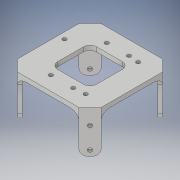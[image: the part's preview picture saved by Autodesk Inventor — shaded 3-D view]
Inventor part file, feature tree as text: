
AUTODESK INVENTOR PART (.ipt)
format: ipt  version: 2019 (Build 230136000, 136)  size: 287,232 bytes
history: native  units: mm
features: sketch x7, projected_geometry x5, hole x4, fillet x4, extrude x3, chamfer x1
ambient origin geometry x8: Origin, YZ Plane, XZ Plane, XY Plane, X Axis, Y Axis, Z Axis, Center Point
bodies: Solid1 (feature_tree)
feature tree (24):
  extrude  "Extrusion1"  Depth=4.0mm
  chamfer  "Chamfer2"  Distance=4.0mm
  extrude  "Extrusion4"  Depth=10.0mm
  hole  "Hole4"  [1 undecoded]
  fillet  "Fillet3"  Radius=19.0mm
  hole  "Hole5"  [1 undecoded]
  fillet  "Fillet4"  Radius=14.0mm
  fillet  "Fillet5"  Radius=19.0mm
  hole  "Hole7"  [1 undecoded]
  extrude  "Extrusion5"  Depth=6.0mm
  fillet  "Fillet6"  Radius=68.6mm
  hole  "Hole8"  [1 undecoded]
  sketch  "Sketch1"  dims[d0=75.0mm d1=75.0mm d2=4.0mm d3=0.0mm]
  sketch  "Sketch11"  dims[d66=10.0mm d67=2.0mm d68=45.0deg d69=3.0mm]
  projected_geometry  "Projected Loop11"
  sketch  "Sketch12"  dims[d70=34.0mm d71=0.0mm d72=14.0mm d73=19.0mm]
  projected_geometry  "Projected Loop12"
  sketch  "Sketch13"  dims[d74=3.5mm d75=6.0mm d76=4.0mm d77=2.0mm d78=90.0deg d79=8.0mm d80=0.0mm d81=4.0mm d82=14.0mm d83=19.0mm]
  projected_geometry  "Projected Loop13"
  sketch  "Sketch15"  dims[d84=3.5mm d85=6.0mm d86=4.0mm d87=2.0mm d88=90.0deg d89=8.0mm d90=0.0mm d91=6.0mm]
  sketch  "Sketch16"  dims[d92=6.0mm d108=53.3mm d109=68.6mm]
  projected_geometry  "Projected Loop15"
  sketch  "Sketch17"  dims[d110=15.3mm d111=2.5mm d112=14.0mm d113=2.5mm d117=2.5mm d118=15.2mm d119=3.5mm d120=6.0mm d121=4.0mm d122=2.0mm d123=90.0deg d124=8.0mm d125=0.0mm d126=35.0mm d127=35.0mm d128=35.0mm d129=0.0mm d130=6.0mm d132=50.0mm d133=50.0mm d134=10.0mm d135=10.0mm d136=3.5mm d137=6.0mm d138=4.0mm d139=2.0mm d140=90.0deg d141=8.0mm d142=0.0mm]
  projected_geometry  "Projected Loop16"
note: 4 required parameter values undecoded (feature->parameter linkage not recoverable at this tier; creation-order binding heuristic only, values carry confidence <= 0.55)
